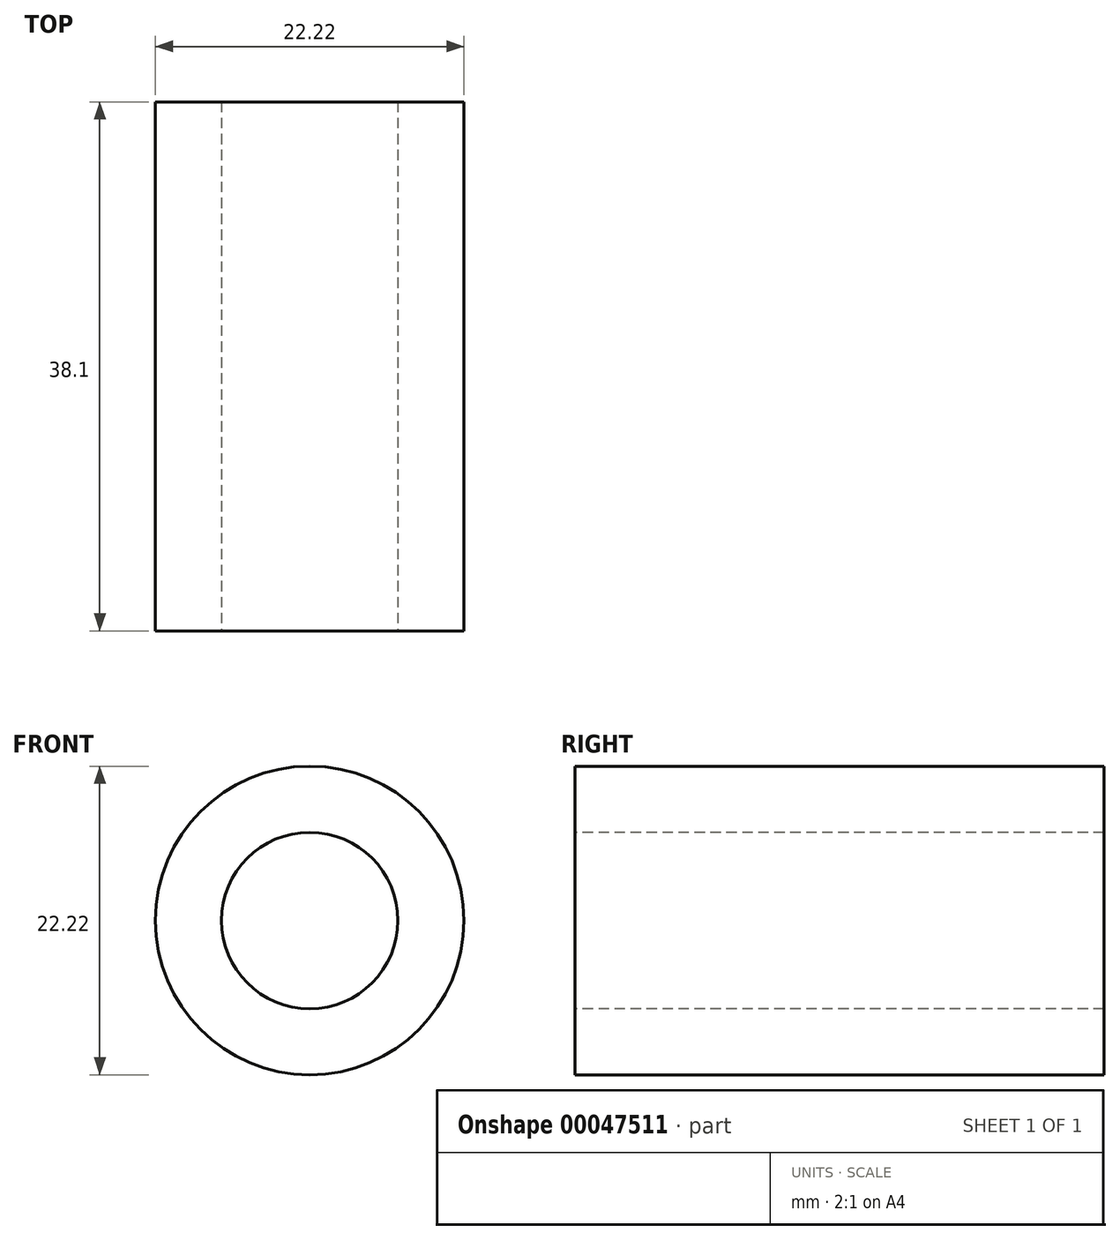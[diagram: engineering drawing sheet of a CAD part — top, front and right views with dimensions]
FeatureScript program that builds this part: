
annotation { "Feature Type Name" : "Feature", "Feature Type Description" : "" }
export const myFeature = defineFeature(function(context is Context, id is Id, definition is map)
    precondition{}
    {
        {
            var Q0;
            Q0=qCreatedBy(makeId("Front.planeOp"),FACE);
            var sketch = newSketch(context, id + "F0", { "sketchPlane" : qUnion([Q0])});
            skCircle(sketch, "E0", {"center": v(0, 0) * mm, "radius": 11.11 * mm});
            skSolve(sketch);
        }
        {
            var Q0;
            Q0=makeQuery(id+"F0.imprint","IMPRINT",FACE,{"disambiguationData":[TD([[makeQuery(id+"F0.imprint","IMPRINT",EDGE,{"derivedFrom":sQuery(id+"F0.wireOp",EDGE,"E0")}),1.0]])]});
            extrude(context, id + "F1", {"entities" : qUnion([Q0]), "endBound" : BoundingType.SYMMETRIC, "depth" : 38.1 * mm});
        }
        {
            var Q0;
            Q0=makeQuery(id+"F1.opExtrude","CAP_FACE",FACE,{"disambiguationData":[OSD([sQuery(id+"F0.wireOp",EDGE,"E0")])],"isStart":false});
            var sketch = newSketch(context, id + "F2", { "sketchPlane" : qUnion([Q0])});
            skCircle(sketch, "E1", {"center": v(0, 0) * mm, "radius": 6.35 * mm});
            skSolve(sketch);
        }
        {
            var Q0;
            Q0=makeQuery(id+"F2.imprint","IMPRINT",FACE,{"disambiguationData":[TD([[makeQuery(id+"F2.imprint","IMPRINT",EDGE,{"derivedFrom":sQuery(id+"F2.wireOp",EDGE,"E1")}),1.0]])]});
            extrude(context, id + "F3", {"entities" : qUnion([Q0]), "operationType" : NewBodyOperationType.REMOVE, "oppositeDirection" : true, "depth" : 38.1 * mm});
        }
    });
